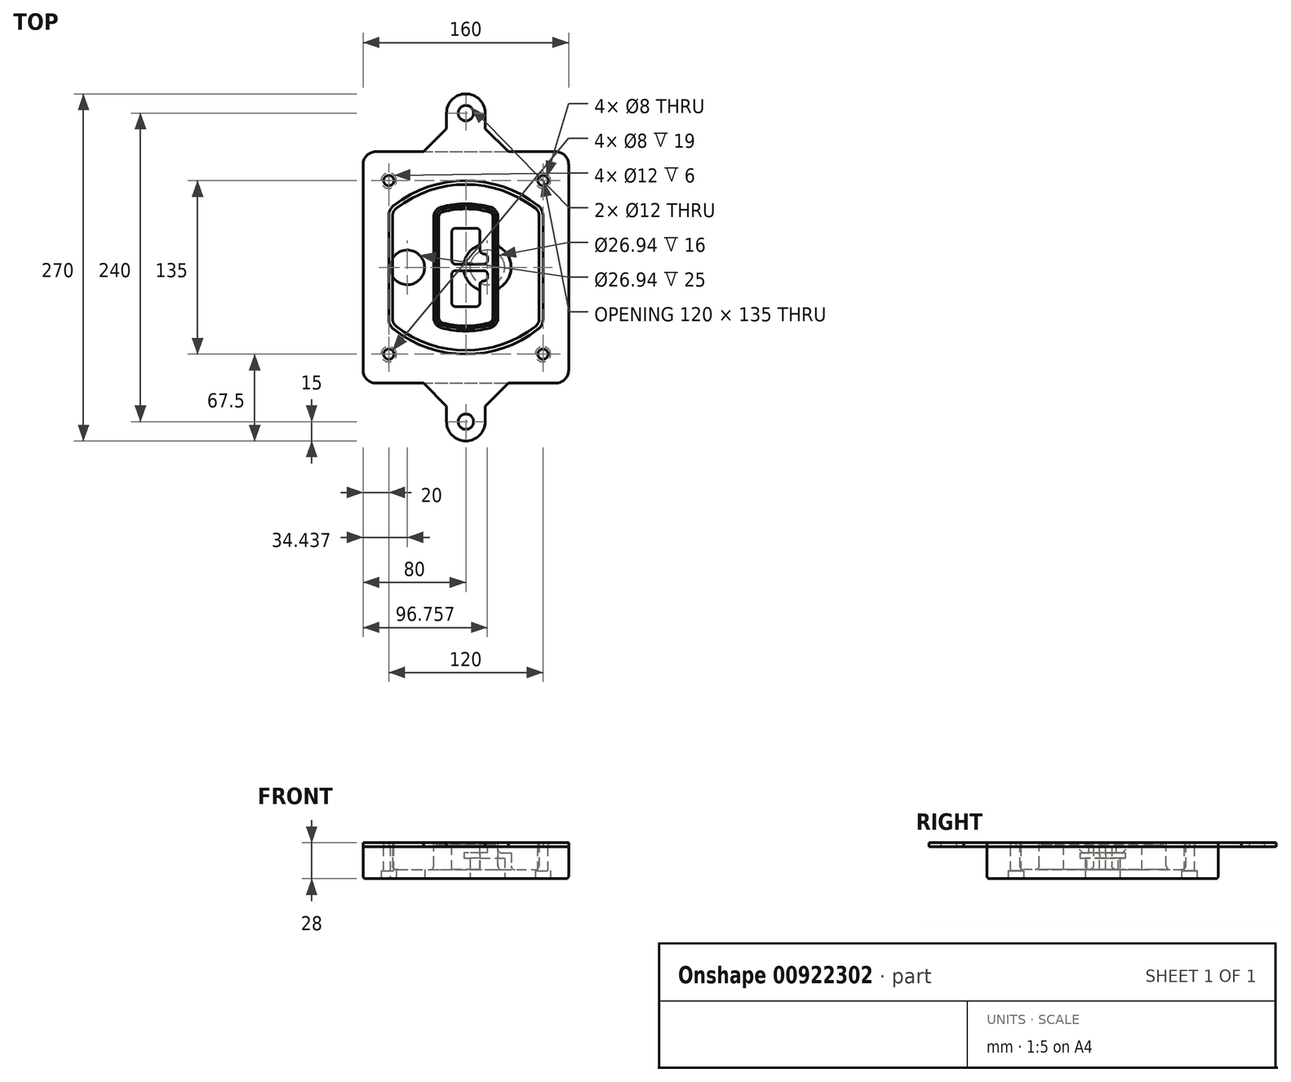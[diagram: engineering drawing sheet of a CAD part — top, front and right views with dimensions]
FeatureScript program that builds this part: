
annotation { "Feature Type Name" : "Feature", "Feature Type Description" : "" }
export const myFeature = defineFeature(function(context is Context, id is Id, definition is map)
    precondition{}
    {
        {
            var Q0;
            Q0=qCreatedBy(makeId("Top.planeOp"),FACE);
            var sketch = newSketch(context, id + "F0", { "sketchPlane" : qUnion([Q0])});
            skPoint(sketch, "E0.rect.middle", {"position": v(0, 0) * mm});
            skLineSegment(sketch, "E1.bottom", {"start": v(-70, -90) * mm, "end": v(70, -90) * mm});
            skLineSegment(sketch, "E1.top", {"start": v(-70, 90) * mm, "end": v(70, 90) * mm});
            skLineSegment(sketch, "E1.left", {"start": v(-80, -80) * mm, "end": v(-80, 80) * mm});
            skLineSegment(sketch, "E1.right", {"start": v(80, -80) * mm, "end": v(80, 80) * mm});
            skLineSegment(sketch, "E2", {"start": v(-80, 90) * mm, "end": v(80, -90) * mm, "construction": true});
            skLineSegment(sketch, "E3", {"start": v(80, 90) * mm, "end": v(-80, -90) * mm, "construction": true});
            skCircle(sketch, "E4", {"center": v(-60, 67.5) * mm, "radius": 4 * mm});
            skCircle(sketch, "E5", {"center": v(60, 67.5) * mm, "radius": 4 * mm});
            skCircle(sketch, "E6", {"center": v(60, -67.5) * mm, "radius": 4 * mm});
            skCircle(sketch, "E7", {"center": v(-60, -67.5) * mm, "radius": 4 * mm});
            skLineSegment(sketch, "E8", {"start": v(-60, 67.5) * mm, "end": v(60, 67.5) * mm, "construction": true});
            skLineSegment(sketch, "E9", {"start": v(60, 67.5) * mm, "end": v(60, -67.5) * mm, "construction": true});
            skLineSegment(sketch, "E10", {"start": v(60, -67.5) * mm, "end": v(-60, -67.5) * mm, "construction": true});
            skLineSegment(sketch, "E11", {"start": v(-60, -67.5) * mm, "end": v(-60, 67.5) * mm, "construction": true});
            skLineSegment(sketch, "E12", {"start": v(-60, 40.3) * mm, "end": v(-60, -40.3) * mm});
            skLineSegment(sketch, "E13", {"start": v(60, 40.3) * mm, "end": v(60, -40.3) * mm});
            skArc(sketch, "E14", {"start": v(56.15, 48.18) * mm, "mid": v(0, 67.5) * mm, "end": v(-56.15, 48.18) * mm});
            skArc(sketch, "E15", {"start": v(-56.15, -48.18) * mm, "mid": v(0, -67.5) * mm, "end": v(56.15, -48.18) * mm});
            skLineSegment(sketch, "E16", {"start": v(-60, 0) * mm, "end": v(60, 0) * mm, "construction": true});
            skPoint(sketch, "E17.visualSharp", {"position": v(-60, -45) * mm});
            skArc(sketch, "E17.filletArc", {"start": v(-60, -40.3) * mm, "mid": v(-58.99, -44.68) * mm, "end": v(-56.15, -48.18) * mm});
            skPoint(sketch, "E18.visualSharp", {"position": v(-60, 45) * mm});
            skArc(sketch, "E18.filletArc", {"start": v(-56.15, 48.18) * mm, "mid": v(-58.99, 44.68) * mm, "end": v(-60, 40.3) * mm});
            skPoint(sketch, "E19.visualSharp", {"position": v(60, 45) * mm});
            skArc(sketch, "E19.filletArc", {"start": v(60, 40.3) * mm, "mid": v(58.99, 44.68) * mm, "end": v(56.15, 48.18) * mm});
            skPoint(sketch, "E20.visualSharp", {"position": v(60, -45) * mm});
            skArc(sketch, "E20.filletArc", {"start": v(56.15, -48.18) * mm, "mid": v(58.99, -44.68) * mm, "end": v(60, -40.3) * mm});
            skPoint(sketch, "E21.visualSharp", {"position": v(-80, 90) * mm});
            skArc(sketch, "E21.filletArc", {"start": v(-70, 90) * mm, "mid": v(-77.07, 87.07) * mm, "end": v(-80, 80) * mm});
            skPoint(sketch, "E22.visualSharp", {"position": v(80, 90) * mm});
            skArc(sketch, "E22.filletArc", {"start": v(80, 80) * mm, "mid": v(77.07, 87.07) * mm, "end": v(70, 90) * mm});
            skPoint(sketch, "E23.visualSharp", {"position": v(80, -90) * mm});
            skArc(sketch, "E23.filletArc", {"start": v(70, -90) * mm, "mid": v(77.07, -87.07) * mm, "end": v(80, -80) * mm});
            skPoint(sketch, "E24.visualSharp", {"position": v(-80, -90) * mm});
            skArc(sketch, "E24.filletArc", {"start": v(-80, -80) * mm, "mid": v(-77.07, -87.07) * mm, "end": v(-70, -90) * mm});
            skArc(sketch, "E25.0", {"start": v(57, 40.3) * mm, "mid": v(56.3, 43.36) * mm, "end": v(54.3, 45.81) * mm});
            skLineSegment(sketch, "E25.1", {"start": v(57, 40.3) * mm, "end": v(57, -40.3) * mm});
            skArc(sketch, "E25.2", {"start": v(54.3, -45.81) * mm, "mid": v(56.3, -43.36) * mm, "end": v(57, -40.3) * mm});
            skArc(sketch, "E25.3", {"start": v(-54.3, -45.81) * mm, "mid": v(0, -64.5) * mm, "end": v(54.3, -45.81) * mm});
            skArc(sketch, "E25.4", {"start": v(-57, -40.3) * mm, "mid": v(-56.3, -43.36) * mm, "end": v(-54.3, -45.81) * mm});
            skArc(sketch, "E25.5", {"start": v(54.3, 45.81) * mm, "mid": v(0, 64.5) * mm, "end": v(-54.3, 45.81) * mm});
            skLineSegment(sketch, "E25.6", {"start": v(-57, 40.3) * mm, "end": v(-57, -40.3) * mm});
            skArc(sketch, "E25.7", {"start": v(-54.3, 45.81) * mm, "mid": v(-56.3, 43.36) * mm, "end": v(-57, 40.3) * mm});
            skArc(sketch, "E26.0", {"start": v(-58.62, 51.33) * mm, "mid": v(-62.58, 46.43) * mm, "end": v(-64, 40.3) * mm});
            skArc(sketch, "E26.1", {"start": v(58.62, 51.33) * mm, "mid": v(0, 71.5) * mm, "end": v(-58.62, 51.33) * mm});
            skArc(sketch, "E26.2", {"start": v(64, 40.3) * mm, "mid": v(62.58, 46.43) * mm, "end": v(58.62, 51.33) * mm});
            skLineSegment(sketch, "E26.3", {"start": v(64, 40.3) * mm, "end": v(64, -40.3) * mm});
            skArc(sketch, "E26.4", {"start": v(58.62, -51.33) * mm, "mid": v(62.58, -46.43) * mm, "end": v(64, -40.3) * mm});
            skLineSegment(sketch, "E26.5", {"start": v(-64, 40.3) * mm, "end": v(-64, -40.3) * mm});
            skArc(sketch, "E26.6", {"start": v(-58.62, -51.33) * mm, "mid": v(0, -71.5) * mm, "end": v(58.62, -51.33) * mm});
            skArc(sketch, "E26.7", {"start": v(-64, -40.3) * mm, "mid": v(-62.58, -46.43) * mm, "end": v(-58.62, -51.33) * mm});
            skSolve(sketch);
        }
        {
            var Q0;
            Q0=makeQuery(id+"F0.imprint","IMPRINT",FACE,{"disambiguationData":[TD([[makeQuery(id+"F0.imprint","IMPRINT",EDGE,{"derivedFrom":sQuery(id+"F0.wireOp",EDGE,"E1.bottom")}),1.0]])]});
            var Q1;
            Q1=makeQuery(id+"F0.imprint","IMPRINT",FACE,{"disambiguationData":[TD([[makeQuery(id+"F0.imprint","IMPRINT",EDGE,{"derivedFrom":sQuery(id+"F0.wireOp",EDGE,"E12")}),1.0]])]});
            var Q2;
            Q2=makeQuery(id+"F0.imprint","IMPRINT",FACE,{"disambiguationData":[TD([[makeQuery(id+"F0.imprint","IMPRINT",EDGE,{"derivedFrom":sQuery(id+"F0.wireOp",EDGE,"E25.0")}),1.0]])]});
            var Q3;
            Q3=makeQuery(id+"F0.imprint","IMPRINT",FACE,{"disambiguationData":[TD([[makeQuery(id+"F0.imprint","IMPRINT",EDGE,{"derivedFrom":sQuery(id+"F0.wireOp",EDGE,"E12")}),-1.0]])]});
            extrude(context, id + "F1", {"entities" : qUnion([Q0, Q1, Q2, Q3]), "oppositeDirection" : true, "depth" : 25 * mm});
        }
        {
            var Q0;
            Q0=makeQuery(id+"F0.imprint","IMPRINT",FACE,{"disambiguationData":[TD([[makeQuery(id+"F0.imprint","IMPRINT",EDGE,{"derivedFrom":sQuery(id+"F0.wireOp",EDGE,"E12")}),1.0]])]});
            extrude(context, id + "F2", {"entities" : qUnion([Q0]), "operationType" : NewBodyOperationType.ADD, "depth" : 3 * mm});
        }
        {
            var Q0;
            Q0=makeQuery(id+"F0.imprint","IMPRINT",FACE,{"disambiguationData":[TD([[makeQuery(id+"F0.imprint","IMPRINT",EDGE,{"derivedFrom":sQuery(id+"F0.wireOp",EDGE,"E25.0")}),1.0]])]});
            extrude(context, id + "F3", {"entities" : qUnion([Q0]), "operationType" : NewBodyOperationType.REMOVE, "oppositeDirection" : true, "depth" : 18 * mm});
        }
        {
            var Q0;
            Q0=makeQuery(id+"F2.opExtrude","CAP_FACE",FACE,{"disambiguationData":[OSD([sQuery(id+"F0.wireOp",EDGE,"E12"),sQuery(id+"F0.wireOp",EDGE,"E13"),sQuery(id+"F0.wireOp",EDGE,"E14"),sQuery(id+"F0.wireOp",EDGE,"E15"),sQuery(id+"F0.wireOp",EDGE,"E17.filletArc"),sQuery(id+"F0.wireOp",EDGE,"E18.filletArc"),sQuery(id+"F0.wireOp",EDGE,"E19.filletArc"),sQuery(id+"F0.wireOp",EDGE,"E20.filletArc"),sQuery(id+"F0.wireOp",EDGE,"E25.0"),sQuery(id+"F0.wireOp",EDGE,"E25.1"),sQuery(id+"F0.wireOp",EDGE,"E25.2"),sQuery(id+"F0.wireOp",EDGE,"E25.3"),sQuery(id+"F0.wireOp",EDGE,"E25.4"),sQuery(id+"F0.wireOp",EDGE,"E25.5"),sQuery(id+"F0.wireOp",EDGE,"E25.6"),sQuery(id+"F0.wireOp",EDGE,"E25.7")])],"isStart":false});
            var sketch = newSketch(context, id + "F4", { "sketchPlane" : qUnion([Q0])});
            skArc(sketch, "E27.0", {"start": v(-19.08, -46.97) * mm, "mid": v(0, -49.5) * mm, "end": v(19.08, -46.97) * mm});
            skArc(sketch, "E28.0", {"start": v(19.08, 46.97) * mm, "mid": v(0, 49.5) * mm, "end": v(-19.08, 46.97) * mm});
            skLineSegment(sketch, "E29", {"start": v(-25, 39.25) * mm, "end": v(-25, -39.25) * mm});
            skLineSegment(sketch, "E30", {"start": v(25, 39.25) * mm, "end": v(25, -39.25) * mm});
            skLineSegment(sketch, "E31", {"start": v(-25, 45.1) * mm, "end": v(25, 45.1) * mm, "construction": true});
            skLineSegment(sketch, "E32", {"start": v(-25, -45.1) * mm, "end": v(25, -45.1) * mm, "construction": true});
            skPoint(sketch, "E33.visualSharp", {"position": v(-25, 45.1) * mm});
            skArc(sketch, "E33.filletArc", {"start": v(-19.08, 46.97) * mm, "mid": v(-23.35, 44.11) * mm, "end": v(-25, 39.25) * mm});
            skPoint(sketch, "E34.visualSharp", {"position": v(25, 45.1) * mm});
            skArc(sketch, "E34.filletArc", {"start": v(25, 39.25) * mm, "mid": v(23.35, 44.11) * mm, "end": v(19.08, 46.97) * mm});
            skPoint(sketch, "E35.visualSharp", {"position": v(25, -45.1) * mm});
            skArc(sketch, "E35.filletArc", {"start": v(19.08, -46.97) * mm, "mid": v(23.35, -44.11) * mm, "end": v(25, -39.25) * mm});
            skPoint(sketch, "E36.visualSharp", {"position": v(-25, -45.1) * mm});
            skArc(sketch, "E36.filletArc", {"start": v(-25, -39.25) * mm, "mid": v(-23.35, -44.11) * mm, "end": v(-19.08, -46.97) * mm});
            skArc(sketch, "E37.0", {"start": v(54.3, 45.81) * mm, "mid": v(0, 64.5) * mm, "end": v(-54.3, 45.81) * mm});
            skArc(sketch, "E37.1", {"start": v(-54.3, 45.81) * mm, "mid": v(-56.3, 43.36) * mm, "end": v(-57, 40.3) * mm});
            skLineSegment(sketch, "E37.2", {"start": v(-57, 40.3) * mm, "end": v(-57, -40.3) * mm});
            skArc(sketch, "E37.3", {"start": v(-57, -40.3) * mm, "mid": v(-56.3, -43.36) * mm, "end": v(-54.3, -45.81) * mm});
            skArc(sketch, "E37.4", {"start": v(-54.3, -45.81) * mm, "mid": v(0, -64.5) * mm, "end": v(54.3, -45.81) * mm});
            skArc(sketch, "E37.5", {"start": v(54.3, -45.81) * mm, "mid": v(56.3, -43.36) * mm, "end": v(57, -40.3) * mm});
            skLineSegment(sketch, "E37.6", {"start": v(57, 40.3) * mm, "end": v(57, -40.3) * mm});
            skArc(sketch, "E37.7", {"start": v(57, 40.3) * mm, "mid": v(56.3, 43.36) * mm, "end": v(54.3, 45.81) * mm});
            skLineSegment(sketch, "E38.0", {"start": v(23, 39.25) * mm, "end": v(23, -39.25) * mm});
            skArc(sketch, "E38.1", {"start": v(18.56, -45.04) * mm, "mid": v(21.76, -42.9) * mm, "end": v(23, -39.25) * mm});
            skArc(sketch, "E38.2", {"start": v(-18.56, -45.04) * mm, "mid": v(0, -47.5) * mm, "end": v(18.56, -45.04) * mm});
            skArc(sketch, "E38.3", {"start": v(-23, -39.25) * mm, "mid": v(-21.76, -42.9) * mm, "end": v(-18.56, -45.04) * mm});
            skLineSegment(sketch, "E38.4", {"start": v(-23, 39.25) * mm, "end": v(-23, -39.25) * mm});
            skArc(sketch, "E38.5", {"start": v(23, 39.25) * mm, "mid": v(21.76, 42.9) * mm, "end": v(18.56, 45.04) * mm});
            skArc(sketch, "E38.6", {"start": v(-18.56, 45.04) * mm, "mid": v(-21.76, 42.9) * mm, "end": v(-23, 39.25) * mm});
            skArc(sketch, "E38.7", {"start": v(18.56, 45.04) * mm, "mid": v(0, 47.5) * mm, "end": v(-18.56, 45.04) * mm});
            skArc(sketch, "E39.0", {"start": v(21, 39.25) * mm, "mid": v(20.18, 41.68) * mm, "end": v(18.04, 43.1) * mm});
            skLineSegment(sketch, "E39.1", {"start": v(21, 39.25) * mm, "end": v(21, -39.25) * mm});
            skArc(sketch, "E39.2", {"start": v(18.04, -43.1) * mm, "mid": v(20.18, -41.68) * mm, "end": v(21, -39.25) * mm});
            skArc(sketch, "E39.3", {"start": v(-18.04, -43.1) * mm, "mid": v(0, -45.5) * mm, "end": v(18.04, -43.1) * mm});
            skArc(sketch, "E39.4", {"start": v(-21, -39.25) * mm, "mid": v(-20.18, -41.68) * mm, "end": v(-18.04, -43.1) * mm});
            skArc(sketch, "E39.5", {"start": v(18.04, 43.1) * mm, "mid": v(0, 45.5) * mm, "end": v(-18.04, 43.1) * mm});
            skLineSegment(sketch, "E39.6", {"start": v(-21, 39.25) * mm, "end": v(-21, -39.25) * mm});
            skArc(sketch, "E39.7", {"start": v(-18.04, 43.1) * mm, "mid": v(-20.18, 41.68) * mm, "end": v(-21, 39.25) * mm});
            skLineSegment(sketch, "E40", {"start": v(-25, 0) * mm, "end": v(25, 0) * mm, "construction": true});
            skLineSegment(sketch, "E41", {"start": v(-11, 5.5) * mm, "end": v(-11, 27.5) * mm});
            skLineSegment(sketch, "E42", {"start": v(-8, 30.5) * mm, "end": v(8, 30.5) * mm});
            skLineSegment(sketch, "E43", {"start": v(11, 27.5) * mm, "end": v(11, 13.5) * mm});
            skLineSegment(sketch, "E44", {"start": v(14, 10.5) * mm, "end": v(14, 10.5) * mm});
            skLineSegment(sketch, "E45", {"start": v(17, 7.5) * mm, "end": v(17, 5.5) * mm});
            skLineSegment(sketch, "E46", {"start": v(14, 2.5) * mm, "end": v(-8, 2.5) * mm});
            skPoint(sketch, "E47.visualSharp", {"position": v(-11, 30.5) * mm});
            skArc(sketch, "E47.filletArc", {"start": v(-8, 30.5) * mm, "mid": v(-10.12, 29.62) * mm, "end": v(-11, 27.5) * mm});
            skPoint(sketch, "E48.visualSharp", {"position": v(11, 30.5) * mm});
            skArc(sketch, "E48.filletArc", {"start": v(11, 27.5) * mm, "mid": v(10.12, 29.62) * mm, "end": v(8, 30.5) * mm});
            skPoint(sketch, "E49.visualSharp", {"position": v(11, 10.5) * mm});
            skArc(sketch, "E49.filletArc", {"start": v(11, 13.5) * mm, "mid": v(11.88, 11.38) * mm, "end": v(14, 10.5) * mm});
            skPoint(sketch, "E50.visualSharp", {"position": v(17, 10.5) * mm});
            skArc(sketch, "E50.filletArc", {"start": v(17, 7.5) * mm, "mid": v(16.12, 9.62) * mm, "end": v(14, 10.5) * mm});
            skPoint(sketch, "E51.visualSharp", {"position": v(17, 2.5) * mm});
            skArc(sketch, "E51.filletArc", {"start": v(14, 2.5) * mm, "mid": v(16.12, 3.38) * mm, "end": v(17, 5.5) * mm});
            skPoint(sketch, "E52.visualSharp", {"position": v(-11, 2.5) * mm});
            skArc(sketch, "E52.filletArc", {"start": v(-11, 5.5) * mm, "mid": v(-10.12, 3.38) * mm, "end": v(-8, 2.5) * mm});
            skLineSegment(sketch, "E53.0.MirrorCS", {"start": v(14, -2.5) * mm, "end": v(-8, -2.5) * mm});
            skArc(sketch, "E54.0.MirrorCS", {"start": v(-11, -5.5) * mm, "mid": v(-10.12, -3.38) * mm, "end": v(-8, -2.5) * mm});
            skLineSegment(sketch, "E55.0.MirrorCS", {"start": v(-11, -5.5) * mm, "end": v(-11, -27.5) * mm});
            skArc(sketch, "E56.0.MirrorCS", {"start": v(-8, -30.5) * mm, "mid": v(-10.12, -29.62) * mm, "end": v(-11, -27.5) * mm});
            skLineSegment(sketch, "E57.0.MirrorCS", {"start": v(-8, -30.5) * mm, "end": v(8, -30.5) * mm});
            skArc(sketch, "E58.0.MirrorCS", {"start": v(11, -27.5) * mm, "mid": v(10.12, -29.62) * mm, "end": v(8, -30.5) * mm});
            skLineSegment(sketch, "E59.0.MirrorCS", {"start": v(11, -27.5) * mm, "end": v(11, -13.5) * mm});
            skArc(sketch, "E60.0.MirrorCS", {"start": v(11, -13.5) * mm, "mid": v(11.88, -11.38) * mm, "end": v(14, -10.5) * mm});
            skArc(sketch, "E61.0.MirrorCS", {"start": v(17, -7.5) * mm, "mid": v(16.12, -9.62) * mm, "end": v(14, -10.5) * mm});
            skLineSegment(sketch, "E62.0.MirrorCS", {"start": v(17, -7.5) * mm, "end": v(17, -5.5) * mm});
            skArc(sketch, "E63.0.MirrorCS", {"start": v(14, -2.5) * mm, "mid": v(16.12, -3.38) * mm, "end": v(17, -5.5) * mm});
            skSolve(sketch);
        }
        {
            var Q0;
            Q0=makeQuery(id+"F4.imprint","IMPRINT",FACE,{"disambiguationData":[TD([[makeQuery(id+"F4.imprint","IMPRINT",EDGE,{"derivedFrom":sQuery(id+"F4.wireOp",EDGE,"E27.0")}),1.0]])]});
            var Q1;
            Q1=makeQuery(id+"F4.imprint","IMPRINT",FACE,{"disambiguationData":[TD([[makeQuery(id+"F4.imprint","IMPRINT",EDGE,{"derivedFrom":sQuery(id+"F4.wireOp",EDGE,"E38.0")}),-1.0]])]});
            var Q2;
            Q2=makeQuery(id+"F4.imprint","IMPRINT",FACE,{"disambiguationData":[TD([[makeQuery(id+"F4.imprint","IMPRINT",EDGE,{"derivedFrom":sQuery(id+"F4.wireOp",EDGE,"E39.0")}),1.0]])]});
            extrude(context, id + "F5", {"entities" : qUnion([Q0, Q1, Q2]), "operationType" : NewBodyOperationType.ADD, "endBound" : BoundingType.UP_TO_NEXT, "oppositeDirection" : true, "depth" : 25 * mm});
        }
        {
            var Q0;
            Q0=makeQuery(id+"F4.imprint","IMPRINT",FACE,{"disambiguationData":[TD([[makeQuery(id+"F4.imprint","IMPRINT",EDGE,{"derivedFrom":sQuery(id+"F4.wireOp",EDGE,"E38.0")}),-1.0]])]});
            extrude(context, id + "F6", {"entities" : qUnion([Q0]), "operationType" : NewBodyOperationType.REMOVE, "oppositeDirection" : true, "depth" : 2 * mm});
        }
        {
            var Q0;
            Q0=makeQuery(id+"F1.opExtrude","CAP_FACE",FACE,{"disambiguationData":[OSD([sQuery(id+"F0.wireOp",EDGE,"E1.bottom"),sQuery(id+"F0.wireOp",EDGE,"E1.top"),sQuery(id+"F0.wireOp",EDGE,"E1.left"),sQuery(id+"F0.wireOp",EDGE,"E1.right"),sQuery(id+"F0.wireOp",EDGE,"E4"),sQuery(id+"F0.wireOp",EDGE,"E5"),sQuery(id+"F0.wireOp",EDGE,"E6"),sQuery(id+"F0.wireOp",EDGE,"E7"),sQuery(id+"F0.wireOp",EDGE,"E21.filletArc"),sQuery(id+"F0.wireOp",EDGE,"E22.filletArc"),sQuery(id+"F0.wireOp",EDGE,"E23.filletArc"),sQuery(id+"F0.wireOp",EDGE,"E24.filletArc")])],"isStart":false});
            var sketch = newSketch(context, id + "F7", { "sketchPlane" : qUnion([Q0])});
            skCircle(sketch, "E64", {"center": v(16.76, 0) * mm, "radius": 13.47 * mm});
            skCircle(sketch, "E65", {"center": v(-45.56, 0) * mm, "radius": 13.47 * mm});
            skLineSegment(sketch, "E66", {"start": v(80, 0) * mm, "end": v(-80, 0) * mm});
            skCircle(sketch, "E67", {"center": v(16.76, 0) * mm, "radius": 18.47 * mm});
            skCircle(sketch, "E68", {"center": v(60, -67.5) * mm, "radius": 6 * mm});
            skCircle(sketch, "E69", {"center": v(-60, -67.5) * mm, "radius": 6 * mm});
            skCircle(sketch, "E70", {"center": v(-60, 67.5) * mm, "radius": 6 * mm});
            skCircle(sketch, "E71", {"center": v(60, 67.5) * mm, "radius": 6 * mm});
            skSolve(sketch);
        }
        {
            var Q0;
            {var subQ1=sQuery(id+"F7.wireOp",EDGE,"E66");var subQ4=sQuery(id+"F7.wireOp",EDGE,"E64");var subQ6=makeQuery(id+"F7.imprint","INTERSECT",VERTEX,{"disambiguationData":[OD(0.0)],"derivedFrom":[subQ4,subQ1]});Q0=makeQuery(id+"F7.imprint","IMPRINT",FACE,{"disambiguationData":[TD([[makeQuery(id+"F7.imprint","IMPRINT",EDGE,{"disambiguationData":[TD([[subQ6,-1.0]])],"derivedFrom":subQ4}),-1.0]])]});}
            var Q1;
            {var subQ0=sQuery(id+"F7.wireOp",EDGE,"E66");var subQ1=sQuery(id+"F7.wireOp",EDGE,"E64");var subQ3=makeQuery(id+"F7.imprint","INTERSECT",VERTEX,{"disambiguationData":[OD(0.0)],"derivedFrom":[subQ1,subQ0]});Q1=makeQuery(id+"F7.imprint","IMPRINT",FACE,{"disambiguationData":[TD([[makeQuery(id+"F7.imprint","IMPRINT",EDGE,{"disambiguationData":[TD([[subQ3,-1.0]])],"derivedFrom":subQ1}),1.0]])]});}
            var Q2;
            {var subQ0=sQuery(id+"F7.wireOp",EDGE,"E66");var subQ1=sQuery(id+"F7.wireOp",EDGE,"E64");var subQ3=makeQuery(id+"F7.imprint","INTERSECT",VERTEX,{"disambiguationData":[OD(0.0)],"derivedFrom":[subQ1,subQ0]});Q2=makeQuery(id+"F7.imprint","IMPRINT",FACE,{"disambiguationData":[TD([[makeQuery(id+"F7.imprint","IMPRINT",EDGE,{"disambiguationData":[TD([[subQ3,1.0]])],"derivedFrom":subQ1}),1.0]])]});}
            var Q3;
            {var subQ1=sQuery(id+"F7.wireOp",EDGE,"E66");var subQ4=sQuery(id+"F7.wireOp",EDGE,"E64");var subQ6=makeQuery(id+"F7.imprint","INTERSECT",VERTEX,{"disambiguationData":[OD(0.0)],"derivedFrom":[subQ4,subQ1]});Q3=makeQuery(id+"F7.imprint","IMPRINT",FACE,{"disambiguationData":[TD([[makeQuery(id+"F7.imprint","IMPRINT",EDGE,{"disambiguationData":[TD([[subQ6,1.0]])],"derivedFrom":subQ4}),-1.0]])]});}
            extrude(context, id + "F8", {"entities" : qUnion([Q0, Q1, Q2, Q3]), "operationType" : NewBodyOperationType.ADD, "oppositeDirection" : true, "depth" : 20 * mm});
        }
        {
            var Q0;
            {var subQ0=sQuery(id+"F7.wireOp",EDGE,"E66");var subQ1=sQuery(id+"F7.wireOp",EDGE,"E64");var subQ3=makeQuery(id+"F7.imprint","INTERSECT",VERTEX,{"disambiguationData":[OD(0.0)],"derivedFrom":[subQ1,subQ0]});Q0=makeQuery(id+"F7.imprint","IMPRINT",FACE,{"disambiguationData":[TD([[makeQuery(id+"F7.imprint","IMPRINT",EDGE,{"disambiguationData":[TD([[subQ3,-1.0]])],"derivedFrom":subQ1}),1.0]])]});}
            var Q1;
            {var subQ0=sQuery(id+"F7.wireOp",EDGE,"E66");var subQ1=sQuery(id+"F7.wireOp",EDGE,"E64");var subQ3=makeQuery(id+"F7.imprint","INTERSECT",VERTEX,{"disambiguationData":[OD(0.0)],"derivedFrom":[subQ1,subQ0]});Q1=makeQuery(id+"F7.imprint","IMPRINT",FACE,{"disambiguationData":[TD([[makeQuery(id+"F7.imprint","IMPRINT",EDGE,{"disambiguationData":[TD([[subQ3,1.0]])],"derivedFrom":subQ1}),1.0]])]});}
            extrude(context, id + "F9", {"entities" : qUnion([Q0, Q1]), "operationType" : NewBodyOperationType.REMOVE, "oppositeDirection" : true, "depth" : 16 * mm});
        }
        {
            var Q0;
            {var subQ0=sQuery(id+"F7.wireOp",EDGE,"E66");var subQ1=sQuery(id+"F7.wireOp",EDGE,"E65");var subQ3=makeQuery(id+"F7.imprint","INTERSECT",VERTEX,{"disambiguationData":[OD(0.0)],"derivedFrom":[subQ1,subQ0]});Q0=makeQuery(id+"F7.imprint","IMPRINT",FACE,{"disambiguationData":[TD([[makeQuery(id+"F7.imprint","IMPRINT",EDGE,{"disambiguationData":[TD([[subQ3,-1.0]])],"derivedFrom":subQ1}),1.0]])]});}
            var Q1;
            {var subQ0=sQuery(id+"F7.wireOp",EDGE,"E66");var subQ1=sQuery(id+"F7.wireOp",EDGE,"E65");var subQ3=makeQuery(id+"F7.imprint","INTERSECT",VERTEX,{"disambiguationData":[OD(0.0)],"derivedFrom":[subQ1,subQ0]});Q1=makeQuery(id+"F7.imprint","IMPRINT",FACE,{"disambiguationData":[TD([[makeQuery(id+"F7.imprint","IMPRINT",EDGE,{"disambiguationData":[TD([[subQ3,1.0]])],"derivedFrom":subQ1}),1.0]])]});}
            extrude(context, id + "F10", {"entities" : qUnion([Q0, Q1]), "operationType" : NewBodyOperationType.REMOVE, "oppositeDirection" : true, "depth" : 25 * mm});
        }
        {
            var Q0;
            Q0=makeQuery(id+"F7.imprint","IMPRINT",FACE,{"disambiguationData":[TD([[makeQuery(id+"F7.imprint","IMPRINT",EDGE,{"derivedFrom":sQuery(id+"F7.wireOp",EDGE,"E68")}),1.0]])]});
            var Q1;
            Q1=makeQuery(id+"F7.imprint","IMPRINT",FACE,{"disambiguationData":[TD([[makeQuery(id+"F7.imprint","IMPRINT",EDGE,{"derivedFrom":makeQuery(id+"F1.opExtrude","CAP_EDGE",EDGE,{"disambiguationData":[OSD([sQuery(id+"F0.wireOp",EDGE,"E5")])],"isStart":false})}),-1.0]])]});
            var Q2;
            Q2=makeQuery(id+"F7.imprint","IMPRINT",FACE,{"disambiguationData":[TD([[makeQuery(id+"F7.imprint","IMPRINT",EDGE,{"derivedFrom":sQuery(id+"F7.wireOp",EDGE,"E69")}),1.0]])]});
            var Q3;
            Q3=makeQuery(id+"F7.imprint","IMPRINT",FACE,{"disambiguationData":[TD([[makeQuery(id+"F7.imprint","IMPRINT",EDGE,{"derivedFrom":makeQuery(id+"F1.opExtrude","CAP_EDGE",EDGE,{"disambiguationData":[OSD([sQuery(id+"F0.wireOp",EDGE,"E4")])],"isStart":false})}),-1.0]])]});
            var Q4;
            Q4=makeQuery(id+"F7.imprint","IMPRINT",FACE,{"disambiguationData":[TD([[makeQuery(id+"F7.imprint","IMPRINT",EDGE,{"derivedFrom":sQuery(id+"F7.wireOp",EDGE,"E70")}),1.0]])]});
            var Q5;
            Q5=makeQuery(id+"F7.imprint","IMPRINT",FACE,{"disambiguationData":[TD([[makeQuery(id+"F7.imprint","IMPRINT",EDGE,{"derivedFrom":makeQuery(id+"F1.opExtrude","CAP_EDGE",EDGE,{"disambiguationData":[OSD([sQuery(id+"F0.wireOp",EDGE,"E7")])],"isStart":false})}),-1.0]])]});
            var Q6;
            Q6=makeQuery(id+"F7.imprint","IMPRINT",FACE,{"disambiguationData":[TD([[makeQuery(id+"F7.imprint","IMPRINT",EDGE,{"derivedFrom":sQuery(id+"F7.wireOp",EDGE,"E71")}),1.0]])]});
            var Q7;
            Q7=makeQuery(id+"F7.imprint","IMPRINT",FACE,{"disambiguationData":[TD([[makeQuery(id+"F7.imprint","IMPRINT",EDGE,{"derivedFrom":makeQuery(id+"F1.opExtrude","CAP_EDGE",EDGE,{"disambiguationData":[OSD([sQuery(id+"F0.wireOp",EDGE,"E6")])],"isStart":false})}),-1.0]])]});
            extrude(context, id + "F11", {"entities" : qUnion([Q0, Q1, Q2, Q3, Q4, Q5, Q6, Q7]), "operationType" : NewBodyOperationType.REMOVE, "oppositeDirection" : true, "depth" : 6 * mm});
        }
        {
            var Q0;
            Q0=makeQuery(id+"F9.boolean.opBoolean","COPY",FACE,{"derivedFrom":makeQuery(id+"F9.opExtrude","CAP_FACE",FACE,{"disambiguationData":[OSD([sQuery(id+"F7.wireOp",EDGE,"E64")])],"isStart":false})});
            var sketch = newSketch(context, id + "F12", { "sketchPlane" : qUnion([Q0])});
            skArc(sketch, "E72.0", {"start": v(11, 17.55) * mm, "mid": v(2.57, 11.82) * mm, "end": v(-1.54, 2.5) * mm});
            skArc(sketch, "E72.1", {"start": v(-1.54, -2.5) * mm, "mid": v(2.57, -11.82) * mm, "end": v(11, -17.55) * mm});
            skLineSegment(sketch, "E73", {"start": v(-1.54, -2.5) * mm, "end": v(14, -2.5) * mm});
            skLineSegment(sketch, "E74.0", {"start": v(14, 2.5) * mm, "end": v(-1.54, 2.5) * mm});
            skArc(sketch, "E74.1", {"start": v(14, 2.5) * mm, "mid": v(16.12, 3.38) * mm, "end": v(17, 5.5) * mm});
            skLineSegment(sketch, "E74.2", {"start": v(17, 7.5) * mm, "end": v(17, 5.5) * mm});
            skArc(sketch, "E74.3", {"start": v(17, 7.5) * mm, "mid": v(16.12, 9.62) * mm, "end": v(14, 10.5) * mm});
            skArc(sketch, "E74.4", {"start": v(11, 13.5) * mm, "mid": v(11.88, 11.38) * mm, "end": v(14, 10.5) * mm});
            skLineSegment(sketch, "E74.5", {"start": v(11, 17.55) * mm, "end": v(11, 13.5) * mm});
            skLineSegment(sketch, "E74.7", {"start": v(14, -2.5) * mm, "end": v(-1.54, -2.5) * mm});
            skArc(sketch, "E74.8", {"start": v(14, -2.5) * mm, "mid": v(16.12, -3.38) * mm, "end": v(17, -5.5) * mm});
            skLineSegment(sketch, "E74.9", {"start": v(17, -7.5) * mm, "end": v(17, -5.5) * mm});
            skArc(sketch, "E74.10", {"start": v(17, -7.5) * mm, "mid": v(16.12, -9.62) * mm, "end": v(14, -10.5) * mm});
            skArc(sketch, "E74.11", {"start": v(11, -13.5) * mm, "mid": v(11.88, -11.38) * mm, "end": v(14, -10.5) * mm});
            skLineSegment(sketch, "E74.12", {"start": v(11, -17.55) * mm, "end": v(11, -13.5) * mm});
            skPoint(sketch, "E75.orphan", {"position": v(11, -27.5) * mm});
            skPoint(sketch, "E76.orphan", {"position": v(-8, -2.5) * mm});
            skPoint(sketch, "E77.orphan", {"position": v(-8, 2.5) * mm});
            skPoint(sketch, "E78.orphan", {"position": v(11, 27.5) * mm});
            skSolve(sketch);
        }
        {
            var Q0;
            {var subQ7=sQuery(id+"F12.wireOp",EDGE,"E72.0");var subQ14=sQuery(id+"F12.wireOp",EDGE,"E72.1");var subQ16=sQuery(id+"F12.wireOp",EDGE,"E74.1");var subQ18=sQuery(id+"F12.wireOp",EDGE,"E74.8");Q0=qUnion([makeQuery(id+"F12.imprint","IMPRINT",FACE,{"disambiguationData":[TD([[makeQuery(id+"F12.imprint","IMPRINT",EDGE,{"derivedFrom":subQ7}),1.0]])]}),makeQuery(id+"F12.imprint","IMPRINT",FACE,{"disambiguationData":[TD([[makeQuery(id+"F12.imprint","IMPRINT",EDGE,{"derivedFrom":subQ14}),1.0]])]}),makeQuery(id+"F12.imprint","IMPRINT",FACE,{"disambiguationData":[TD([[makeQuery(id+"F12.imprint","IMPRINT",EDGE,{"derivedFrom":subQ16}),1.0]])]}),makeQuery(id+"F12.imprint","IMPRINT",FACE,{"disambiguationData":[TD([[makeQuery(id+"F12.imprint","IMPRINT",EDGE,{"derivedFrom":subQ18}),-1.0]])]})]);}
            var Q1;
            Q1=makeQuery(id+"F5.boolean.opBoolean","SPLIT",FACE,{"disambiguationData":[TD([makeQuery(id+"F5.opExtrude","SWEPT_FACE",FACE,{"disambiguationData":[OSD([sQuery(id+"F4.wireOp",EDGE,"E41")])]})])],"derivedFrom":makeQuery(id+"F3.boolean.opBoolean","COPY",FACE,{"derivedFrom":makeQuery(id+"F3.opExtrude","CAP_FACE",FACE,{"disambiguationData":[OSD([sQuery(id+"F0.wireOp",EDGE,"E25.0"),sQuery(id+"F0.wireOp",EDGE,"E25.1"),sQuery(id+"F0.wireOp",EDGE,"E25.2"),sQuery(id+"F0.wireOp",EDGE,"E25.3"),sQuery(id+"F0.wireOp",EDGE,"E25.4"),sQuery(id+"F0.wireOp",EDGE,"E25.5"),sQuery(id+"F0.wireOp",EDGE,"E25.6"),sQuery(id+"F0.wireOp",EDGE,"E25.7")])],"isStart":false})})});
            extrude(context, id + "F13", {"entities" : qUnion([Q0]), "operationType" : NewBodyOperationType.REMOVE, "endBound" : BoundingType.UP_TO_SURFACE, "endBoundEntityFace" : qUnion([Q1]), "depth" : 25 * mm});
        }
        {
            var Q0;
            Q0=makeQuery(id+"F3.boolean.opBoolean","COPY",EDGE,{"derivedFrom":makeQuery(id+"F3.opExtrude","CAP_EDGE",EDGE,{"disambiguationData":[OSD([sQuery(id+"F0.wireOp",EDGE,"E25.6")])],"isStart":false})});
            var Q1;
            Q1=makeQuery(id+"F8.boolean.opBoolean","INTERSECT",EDGE,{"derivedFrom":[makeQuery(id+"F5.opExtrude","SWEPT_FACE",FACE,{"disambiguationData":[OSD([sQuery(id+"F4.wireOp",EDGE,"E30")])]}),makeQuery(id+"F8.opExtrude","CAP_FACE",FACE,{"disambiguationData":[OSD([sQuery(id+"F7.wireOp",EDGE,"E67")])],"isStart":false})]});
            var Q2;
            Q2=makeQuery(id+"F8.boolean.opBoolean","INTERSECT",EDGE,{"disambiguationData":[OD(1.0)],"derivedFrom":[makeQuery(id+"F5.opExtrude","SWEPT_FACE",FACE,{"disambiguationData":[OSD([sQuery(id+"F4.wireOp",EDGE,"E30")])]}),makeQuery(id+"F8.opExtrude","SWEPT_FACE",FACE,{"disambiguationData":[OSD([sQuery(id+"F7.wireOp",EDGE,"E67")])]})]});
            var Q3;
            {var subQ0=sQuery(id+"F4.wireOp",EDGE,"E30");Q3=makeQuery(id+"F8.boolean.opBoolean","SPLIT",EDGE,{"disambiguationData":[TD([makeQuery(id+"F5.opExtrude","SWEPT_FACE",FACE,{"disambiguationData":[OSD([sQuery(id+"F4.wireOp",EDGE,"E35.filletArc")])]})])],"derivedFrom":makeQuery(id+"F5.opExtrude","CAP_EDGE",EDGE,{"disambiguationData":[OSD([subQ0])],"isStart":false})});}
            var Q4;
            {var subQ0=sQuery(id+"F0.wireOp",EDGE,"E25.7");var subQ1=sQuery(id+"F0.wireOp",EDGE,"E25.1");var subQ2=sQuery(id+"F0.wireOp",EDGE,"E25.6");var subQ3=sQuery(id+"F0.wireOp",EDGE,"E25.5");var subQ4=sQuery(id+"F0.wireOp",EDGE,"E25.4");var subQ5=sQuery(id+"F0.wireOp",EDGE,"E25.0");var subQ6=sQuery(id+"F0.wireOp",EDGE,"E25.2");var subQ7=sQuery(id+"F0.wireOp",EDGE,"E25.3");Q4=makeQuery(id+"F8.boolean.opBoolean","INTERSECT",EDGE,{"derivedFrom":[makeQuery(id+"F5.boolean.opBoolean","SPLIT",FACE,{"disambiguationData":[TD([makeQuery(id+"F2.opExtrude","SWEPT_FACE",FACE,{"disambiguationData":[OSD([subQ5])]})])],"derivedFrom":makeQuery(id+"F3.boolean.opBoolean","COPY",FACE,{"derivedFrom":makeQuery(id+"F3.opExtrude","CAP_FACE",FACE,{"disambiguationData":[OSD([subQ5,subQ1,subQ6,subQ7,subQ4,subQ3,subQ2,subQ0])],"isStart":false})})}),makeQuery(id+"F8.opExtrude","SWEPT_FACE",FACE,{"disambiguationData":[OSD([sQuery(id+"F7.wireOp",EDGE,"E67")])]})]});}
            var Q5;
            Q5=makeQuery(id+"F8.boolean.opBoolean","INTERSECT",EDGE,{"disambiguationData":[OD(0.0)],"derivedFrom":[makeQuery(id+"F5.opExtrude","SWEPT_FACE",FACE,{"disambiguationData":[OSD([sQuery(id+"F4.wireOp",EDGE,"E30")])]}),makeQuery(id+"F8.opExtrude","SWEPT_FACE",FACE,{"disambiguationData":[OSD([sQuery(id+"F7.wireOp",EDGE,"E67")])]})]});
            fillet(context, id + "F14", {"entities" : qUnion([Q0, Q1, Q2, Q3, Q4, Q5]), "radius" : 3 * mm, "tangentPropagation" : true, "allowEdgeOverflow" : false});
        }
        {
            var Q0;
            Q0=makeQuery(id+"F1.opExtrude","CAP_EDGE",EDGE,{"disambiguationData":[OSD([sQuery(id+"F0.wireOp",EDGE,"E1.bottom")])],"isStart":false});
            fillet(context, id + "F15", {"entities" : qUnion([Q0]), "radius" : 2 * mm, "tangentPropagation" : true, "allowEdgeOverflow" : false});
        }
        {
            var Q0;
            {var subQ0=sQuery(id+"F0.wireOp",EDGE,"E21.filletArc");var subQ1=sQuery(id+"F0.wireOp",EDGE,"E7");var subQ2=sQuery(id+"F0.wireOp",EDGE,"E6");var subQ3=sQuery(id+"F0.wireOp",EDGE,"E5");var subQ4=sQuery(id+"F0.wireOp",EDGE,"E4");var subQ5=sQuery(id+"F0.wireOp",EDGE,"E22.filletArc");var subQ6=sQuery(id+"F0.wireOp",EDGE,"E1.bottom");var subQ7=sQuery(id+"F0.wireOp",EDGE,"E1.right");var subQ8=sQuery(id+"F0.wireOp",EDGE,"E1.top");var subQ9=sQuery(id+"F0.wireOp",EDGE,"E1.left");var subQ10=sQuery(id+"F0.wireOp",EDGE,"E23.filletArc");var subQ11=sQuery(id+"F0.wireOp",EDGE,"E24.filletArc");Q0=makeQuery(id+"F2.boolean.opBoolean","SPLIT",FACE,{"disambiguationData":[TD([makeQuery(id+"F1.opExtrude","SWEPT_FACE",FACE,{"disambiguationData":[OSD([subQ6])]})])],"derivedFrom":makeQuery(id+"F1.opExtrude","CAP_FACE",FACE,{"disambiguationData":[OSD([subQ6,subQ8,subQ9,subQ7,subQ4,subQ3,subQ2,subQ1,subQ0,subQ5,subQ10,subQ11])],"isStart":true})});}
            var sketch = newSketch(context, id + "F16", { "sketchPlane" : qUnion([Q0])});
            skLineSegment(sketch, "E79.0.0", {"start": v(70, 90) * mm, "end": v(-70, 90) * mm});
            skArc(sketch, "E79.0.1", {"start": v(-70, 90) * mm, "mid": v(-77.07, 87.07) * mm, "end": v(-80, 80) * mm});
            skLineSegment(sketch, "E79.0.2", {"start": v(-80, 80) * mm, "end": v(-80, -80) * mm});
            skArc(sketch, "E79.0.3", {"start": v(-80, -80) * mm, "mid": v(-77.07, -87.07) * mm, "end": v(-70, -90) * mm});
            skLineSegment(sketch, "E79.0.4", {"start": v(-70, -90) * mm, "end": v(70, -90) * mm});
            skArc(sketch, "E79.0.5", {"start": v(70, -90) * mm, "mid": v(77.07, -87.07) * mm, "end": v(80, -80) * mm});
            skLineSegment(sketch, "E79.0.6", {"start": v(80, -80) * mm, "end": v(80, 80) * mm});
            skArc(sketch, "E79.0.7", {"start": v(80, 80) * mm, "mid": v(77.07, 87.07) * mm, "end": v(70, 90) * mm});
            skCircle(sketch, "E80.0", {"center": v(-60, 67.5) * mm, "radius": 4 * mm});
            skCircle(sketch, "E81.0", {"center": v(60, 67.5) * mm, "radius": 4 * mm});
            skCircle(sketch, "E82.0", {"center": v(60, -67.5) * mm, "radius": 4 * mm});
            skCircle(sketch, "E83.0", {"center": v(-60, -67.5) * mm, "radius": 4 * mm});
            skLineSegment(sketch, "E84.0.0", {"start": v(60, -40.3) * mm, "end": v(60, 40.3) * mm});
            skArc(sketch, "E84.0.1", {"start": v(60, 40.3) * mm, "mid": v(58.99, 44.68) * mm, "end": v(56.15, 48.18) * mm});
            skArc(sketch, "E84.0.2", {"start": v(56.15, 48.18) * mm, "mid": v(0, 67.5) * mm, "end": v(-56.15, 48.18) * mm});
            skArc(sketch, "E84.0.3", {"start": v(-56.15, 48.18) * mm, "mid": v(-58.99, 44.68) * mm, "end": v(-60, 40.3) * mm});
            skLineSegment(sketch, "E84.0.4", {"start": v(-60, 40.3) * mm, "end": v(-60, -40.3) * mm});
            skArc(sketch, "E84.0.5", {"start": v(-60, -40.3) * mm, "mid": v(-58.99, -44.68) * mm, "end": v(-56.15, -48.18) * mm});
            skArc(sketch, "E84.0.6", {"start": v(-56.15, -48.18) * mm, "mid": v(0, -67.5) * mm, "end": v(56.15, -48.18) * mm});
            skArc(sketch, "E84.0.7", {"start": v(56.15, -48.18) * mm, "mid": v(58.99, -44.68) * mm, "end": v(60, -40.3) * mm});
            skLineSegment(sketch, "E85", {"start": v(0, 90) * mm, "end": v(0, 120) * mm, "construction": true});
            skCircle(sketch, "E86", {"center": v(0, 120) * mm, "radius": 6 * mm});
            skLineSegment(sketch, "E87", {"start": v(-33, 90) * mm, "end": v(-15, 108) * mm});
            skLineSegment(sketch, "E88", {"start": v(-15, 108) * mm, "end": v(-15, 120) * mm});
            skArc(sketch, "E89", {"start": v(15, 120) * mm, "mid": v(0, 135) * mm, "end": v(-15, 120) * mm});
            skLineSegment(sketch, "E90.MirrorCS", {"start": v(15, 108) * mm, "end": v(15, 120) * mm});
            skLineSegment(sketch, "E91.MirrorCS", {"start": v(33, 90) * mm, "end": v(15, 108) * mm});
            skLineSegment(sketch, "E92", {"start": v(-80, 0) * mm, "end": v(80, 0) * mm, "construction": true});
            skLineSegment(sketch, "E93.MirrorCS", {"start": v(33, -90) * mm, "end": v(15, -108) * mm});
            skLineSegment(sketch, "E94.MirrorCS", {"start": v(15, -108) * mm, "end": v(15, -120) * mm});
            skArc(sketch, "E95.MirrorCS", {"start": v(15, -120) * mm, "mid": v(0, -135) * mm, "end": v(-15, -120) * mm});
            skCircle(sketch, "E96.MirrorC", {"center": v(0, -120) * mm, "radius": 6 * mm});
            skLineSegment(sketch, "E97.MirrorCS", {"start": v(-15, -108) * mm, "end": v(-15, -120) * mm});
            skLineSegment(sketch, "E98.MirrorCS", {"start": v(-33, -90) * mm, "end": v(-15, -108) * mm});
            skLineSegment(sketch, "E99.MirrorCS", {"start": v(0, -90) * mm, "end": v(0, -120) * mm, "construction": true});
            skSolve(sketch);
        }
        {
            var Q0;
            Q0=makeQuery(id+"F16.imprint","IMPRINT",FACE,{"disambiguationData":[TD([[makeQuery(id+"F16.imprint","IMPRINT",EDGE,{"derivedFrom":sQuery(id+"F16.wireOp",EDGE,"E86")}),-1.0]])]});
            var Q1;
            {var subQ0=sQuery(id+"F16.wireOp",EDGE,"E93.MirrorCS");Q1=makeQuery(id+"F16.imprint","IMPRINT",FACE,{"disambiguationData":[TD([[makeQuery(id+"F16.imprint","IMPRINT",EDGE,{"derivedFrom":subQ0}),-1.0]])]});}
            var Q2;
            {var subQ1=sQuery(id+"F16.wireOp",EDGE,"E79.0.1");Q2=makeQuery(id+"F16.imprint","IMPRINT",FACE,{"disambiguationData":[TD([[makeQuery(id+"F16.imprint","IMPRINT",EDGE,{"derivedFrom":subQ1}),1.0]])]});}
            var Q3;
            Q3=makeQuery(id+"F2.opExtrude","CAP_FACE",FACE,{"disambiguationData":[OSD([sQuery(id+"F0.wireOp",EDGE,"E12"),sQuery(id+"F0.wireOp",EDGE,"E13"),sQuery(id+"F0.wireOp",EDGE,"E14"),sQuery(id+"F0.wireOp",EDGE,"E15"),sQuery(id+"F0.wireOp",EDGE,"E17.filletArc"),sQuery(id+"F0.wireOp",EDGE,"E18.filletArc"),sQuery(id+"F0.wireOp",EDGE,"E19.filletArc"),sQuery(id+"F0.wireOp",EDGE,"E20.filletArc"),sQuery(id+"F0.wireOp",EDGE,"E25.0"),sQuery(id+"F0.wireOp",EDGE,"E25.1"),sQuery(id+"F0.wireOp",EDGE,"E25.2"),sQuery(id+"F0.wireOp",EDGE,"E25.3"),sQuery(id+"F0.wireOp",EDGE,"E25.4"),sQuery(id+"F0.wireOp",EDGE,"E25.5"),sQuery(id+"F0.wireOp",EDGE,"E25.6"),sQuery(id+"F0.wireOp",EDGE,"E25.7")])],"isStart":false});
            extrude(context, id + "F17", {"entities" : qUnion([Q0, Q1, Q2]), "endBound" : BoundingType.UP_TO_SURFACE, "depth" : 25 * mm, "endBoundEntityFace" : qUnion([Q3]), "offsetDistance" : 25 * mm});
        }
    });
